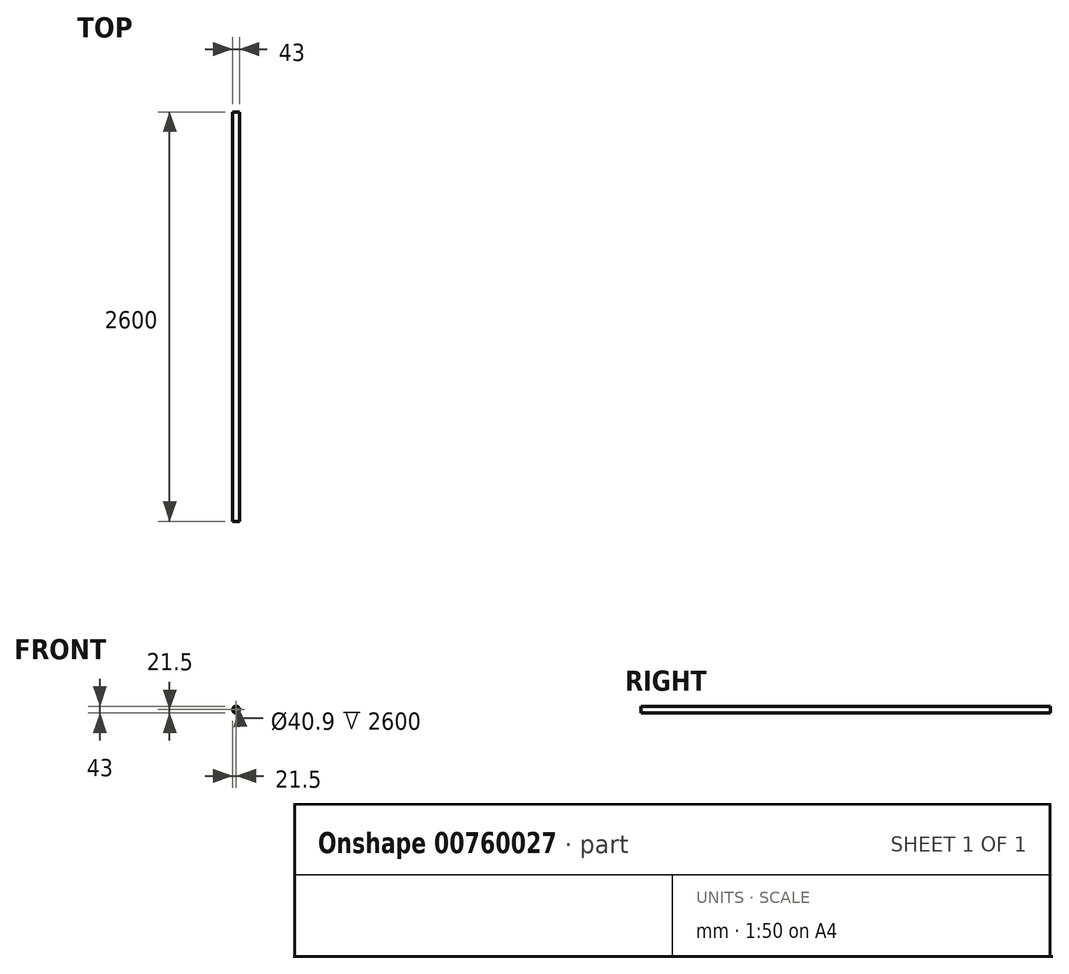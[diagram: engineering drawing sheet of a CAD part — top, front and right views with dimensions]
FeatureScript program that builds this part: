
annotation { "Feature Type Name" : "Feature", "Feature Type Description" : "" }
export const myFeature = defineFeature(function(context is Context, id is Id, definition is map)
    precondition{}
    {
        {
            assignVariable(context, id + "F0", {"name" : "LENGTH", "anyValue" : 2600});
        }
        {
            var Q0;
            Q0=qCreatedBy(makeId("Front.planeOp"),FACE);
            var sketch = newSketch(context, id + "F1", { "sketchPlane" : qUnion([Q0])});
            skCircle(sketch, "E0", {"center": v(0, 0) * mm, "radius": 20.45 * mm});
            skCircle(sketch, "E1", {"center": v(0, 0) * mm, "radius": 21.5 * mm});
            skSolve(sketch);
        }
        {
            var Q0;
            Q0=makeQuery(id+"F1.imprint","IMPRINT",FACE,{"disambiguationData":[TD([[makeQuery(id+"F1.imprint","IMPRINT",EDGE,{"derivedFrom":sQuery(id+"F1.wireOp",EDGE,"E0")}),-1.0]])]});
            extrude(context, id + "F2", {"entities" : qUnion([Q0]), "depth" : (getVariable(context, 'LENGTH')) * mm, "offsetDistance" : 25 * mm});
        }
    });
